# Revit family: Clark Pete Evans Alfresco Single Bowl Undermount
name_source: partatom
category: Plumbing Fixtures
revit_build: Autodesk Revit Architecture 2014 (Build: 20130308_1515(x64)
units: mm (PartAtom-declared; Revit-internal decimal feet)

## types (1)
- Standard
    Assembly Code = D2010410
    Bowl Depth = 209 mm
    CW Connection = No
    Cost = 0 $
    Default Elevation = 0 mm  [stored 0 ft]
    Description = PETE EVANS ALFRESCO SINGLE BOWL UNDERMOUNT
    HW Connection = No
    Keynote = SK
    Manufacturer = Clark
    Material_ANZRS = Metal-Chrome-Caroma
    Model = 6650
    PlumbingMaterial_ANZRS = PVC-White-Caroma
    Type Comments = Includes basket waste, timber board, alfresco mutli-bowl & alfresco bbq tray • Bowl volume: 28.5L • Carton size: 480L x 415W x 390H • Carton weight: 11kg • Exclusive Australian design • Match with Dorf Jovian mixer range
    URL = http://www.clark.com.au
    Vent Connection = No
    WFU = 2
    Waste = Metal-Chrome-Caroma
    Waste Connection = Yes

note: [stored X ft] marks values corroborated as IEEE doubles in the binary element streams (Revit-internal decimal feet)

## geometry (parser evidence)
native form markers: Blend x16, Sweep x5
no freeform markers — native parametric forms only
